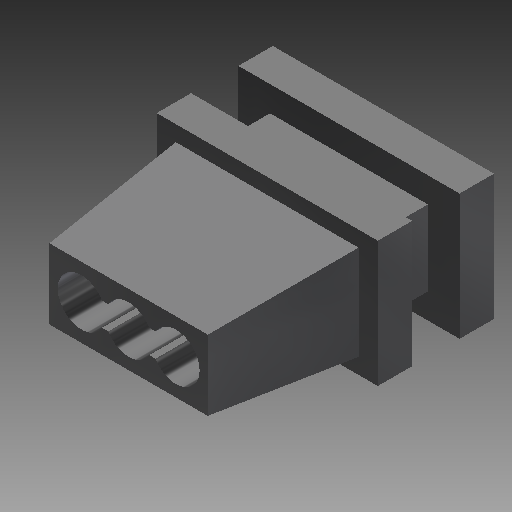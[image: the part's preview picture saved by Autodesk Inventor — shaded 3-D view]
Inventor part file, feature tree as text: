
AUTODESK INVENTOR PART (.ipt)
format: ipt  version: 2018 (Build 220112000, 112)  size: 144,384 bytes
history: native  units: in
note: dims shown in document units (in); Inventor stores cm internally (conversion verified against a paired STEP export)
features: extrude x4, sketch x4, pattern_linear x1, projected_geometry x1
ambient origin geometry x8: Origin, YZ Plane, XZ Plane, XY Plane, X Axis, Y Axis, Z Axis, Center Point
bodies: Solid1 (feature_tree)
feature tree (10):
  extrude  "Extrusion1"  Depth=0.157in
  extrude  "Extrusion2"  Depth=0.197in
  pattern_linear  "Rectangular Pattern1"  Count1=2 Spacing1=0.102in
  extrude  "Extrusion3"  Depth=0.173in
  extrude  "Extrusion4"  Depth=0.173in
  sketch  "Sketch1"  dims[d0=0.276in d1=0.157in]
  sketch  "Sketch2"  dims[d2=0.043in d3=0.0in d4=0.197in]
  sketch  "Sketch3"  dims[d5=0.094in]
  sketch  "Sketch4"  dims[d6=0.059in d7=0.0in d8=0.7874in d10=0.102in d11=0.173in d12=-0.0344in d14=0.228in d15=0.118in d16=0.173in d17=0.0in]
  projected_geometry  "Projected Loop1"
